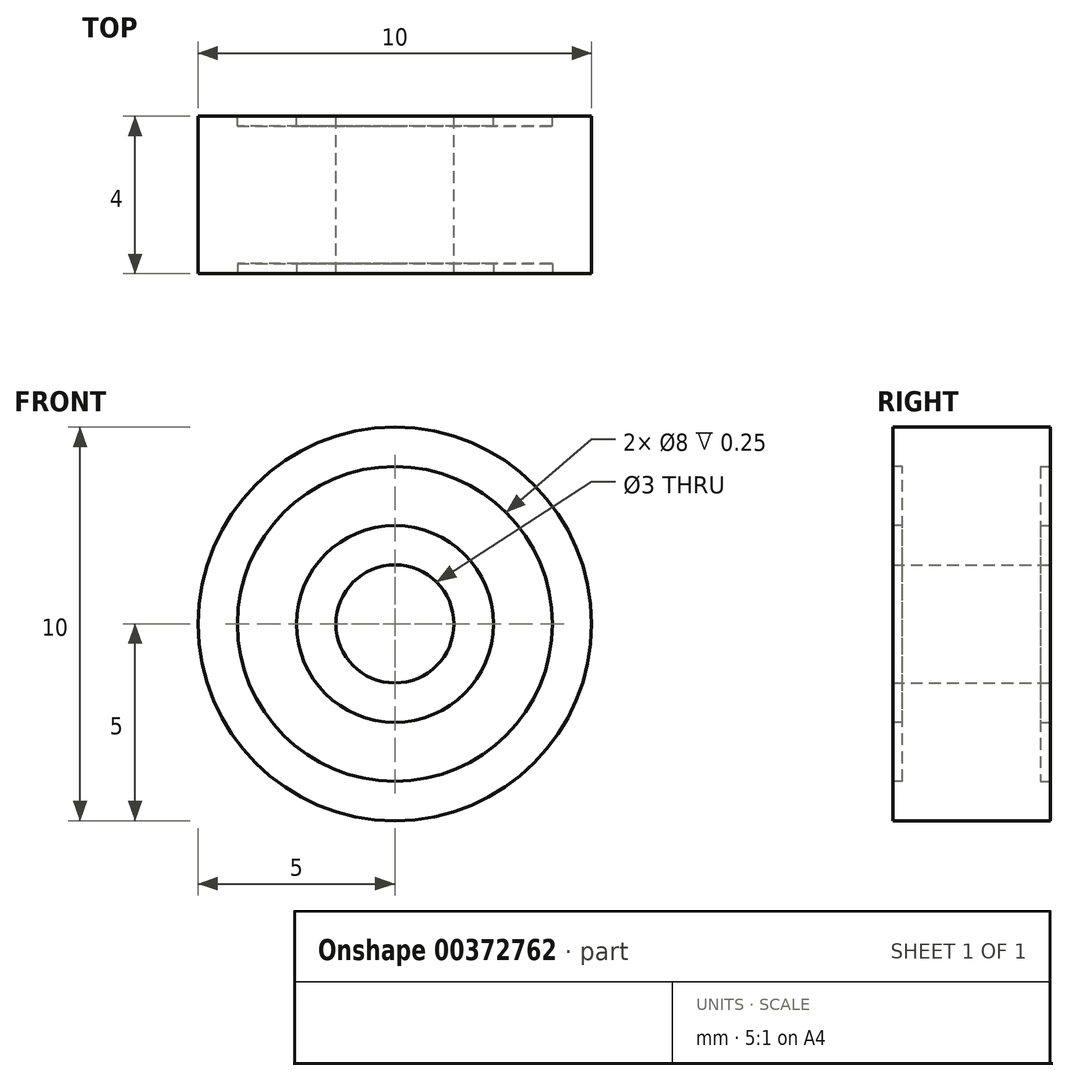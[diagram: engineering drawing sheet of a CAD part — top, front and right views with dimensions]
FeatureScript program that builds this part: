
annotation { "Feature Type Name" : "Feature", "Feature Type Description" : "" }
export const myFeature = defineFeature(function(context is Context, id is Id, definition is map)
    precondition{}
    {
        {
            var Q0;
            Q0=qCreatedBy(makeId("Front.planeOp"),FACE);
            var sketch = newSketch(context, id + "F0", { "sketchPlane" : qUnion([Q0])});
            skCircle(sketch, "E0", {"center": v(0, 0) * mm, "radius": 5 * mm});
            skCircle(sketch, "E1", {"center": v(0, 0) * mm, "radius": 1.5 * mm});
            skSolve(sketch);
        }
        {
            var Q0;
            Q0=qSketchRegion(id+"F0",true);
            extrude(context, id + "F1", {"entities" : qUnion([Q0]), "depth" : 4 * mm, "symmetric" : true});
        }
        {
            var Q0;
            Q0=makeQuery(id+"F1.opExtrude","CAP_FACE",FACE,{"disambiguationData":[OSD([sQuery(id+"F0.wireOp",EDGE,"E0"),sQuery(id+"F0.wireOp",EDGE,"E1")])],"isStart":false});
            var sketch = newSketch(context, id + "F2", { "sketchPlane" : qUnion([Q0])});
            skCircle(sketch, "E2", {"center": v(0, 0) * mm, "radius": 2.5 * mm});
            skCircle(sketch, "E3", {"center": v(0, 0) * mm, "radius": 4 * mm});
            skSolve(sketch);
        }
        {
            var Q0;
            Q0=qSketchRegion(id+"F2",true);
            extrude(context, id + "F3", {"entities" : qUnion([Q0]), "operationType" : NewBodyOperationType.REMOVE, "oppositeDirection" : true, "offsetDistance" : 25 * mm, "depth" : 0.25 * mm});
        }
        {
            var Q0;
            Q0=makeQuery(id+"F1.opExtrude","CAP_FACE",FACE,{"disambiguationData":[OSD([sQuery(id+"F0.wireOp",EDGE,"E0"),sQuery(id+"F0.wireOp",EDGE,"E1")])],"isStart":true});
            var sketch = newSketch(context, id + "F4", { "sketchPlane" : qUnion([Q0])});
            skCircle(sketch, "E4.0", {"center": v(0, 0) * mm, "radius": 2.5 * mm});
            skCircle(sketch, "E5.0", {"center": v(0, 0) * mm, "radius": 4 * mm});
            skSolve(sketch);
        }
        {
            var Q0;
            Q0 = qSketchRegion(id + "F4", true);
            extrude(context, id + "F5", {"entities" : qUnion([Q0]), "operationType" : NewBodyOperationType.REMOVE, "oppositeDirection" : true, "depth" : 0.25 * mm, "offsetDistance" : 25 * mm});
        }
    });
